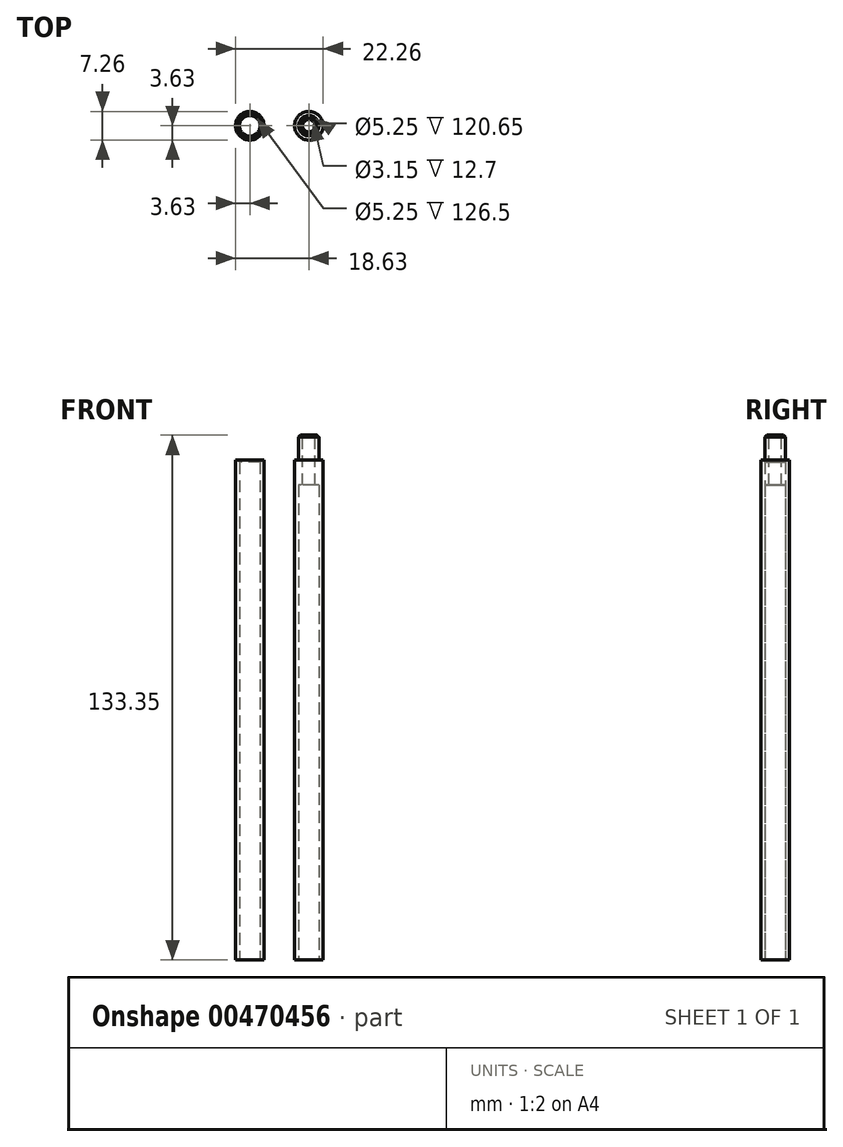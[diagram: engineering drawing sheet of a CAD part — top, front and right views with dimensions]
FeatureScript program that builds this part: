
annotation { "Feature Type Name" : "Feature", "Feature Type Description" : "" }
export const myFeature = defineFeature(function(context is Context, id is Id, definition is map)
    precondition{}
    {
        {
            var Q0;
            Q0=qCreatedBy(makeId("Top.planeOp"),FACE);
            var sketch = newSketch(context, id + "F0", { "sketchPlane" : qUnion([Q0])});
            skCircle(sketch, "E0", {"center": v(7.5, 0) * mm, "radius": 2.62 * mm});
            skCircle(sketch, "E1", {"center": v(-7.5, 0) * mm, "radius": 2.62 * mm});
            skCircle(sketch, "E2", {"center": v(-7.5, 0) * mm, "radius": 3.62 * mm});
            skCircle(sketch, "E3", {"center": v(7.5, 0) * mm, "radius": 3.62 * mm});
            skLineSegment(sketch, "E4", {"start": v(-7.5, 0) * mm, "end": v(7.5, 0) * mm, "construction": true});
            skSolve(sketch);
        }
        {
            var Q0;
            Q0 = qSketchRegion(id + "F0", true);
            extrude(context, id + "F1", {"entities" : qUnion([Q0]), "depth" : 127 * mm});
        }
        {
            var Q0;
            Q0=makeQuery(id+"F1.opExtrude","CAP_FACE",FACE,{"disambiguationData":[OSD([sQuery(id+"F0.wireOp",EDGE,"E0"),sQuery(id+"F0.wireOp",EDGE,"E3")])],"isStart":false});
            var sketch = newSketch(context, id + "F2", { "sketchPlane" : qUnion([Q0])});
            skCircle(sketch, "E5.0", {"center": v(7.5, 0) * mm, "radius": 2.62 * mm});
            skCircle(sketch, "E6", {"center": v(7.5, 0) * mm, "radius": 1.57 * mm});
            skSolve(sketch);
        }
        {
            var Q0;
            Q0 = qSketchRegion(id + "F2", true);
            extrude(context, id + "F3", {"entities" : qUnion([Q0]), "operationType" : NewBodyOperationType.ADD, "oppositeDirection" : true, "depth" : 6.35 * mm});
        }
        {
            var Q0;
            Q0=makeQuery(id+"F3.boolean.opBoolean","MERGE",FACE,{"derivedFrom":[makeQuery(id+"F1.opExtrude","CAP_FACE",FACE,{"disambiguationData":[OSD([sQuery(id+"F0.wireOp",EDGE,"E0"),sQuery(id+"F0.wireOp",EDGE,"E3")])],"isStart":false}),makeQuery(id+"F3.opExtrude","CAP_FACE",FACE,{"disambiguationData":[OSD([sQuery(id+"F2.wireOp",EDGE,"E5.0"),sQuery(id+"F2.wireOp",EDGE,"E6")])],"isStart":true})]});
            var sketch = newSketch(context, id + "F4", { "sketchPlane" : qUnion([Q0])});
            skCircle(sketch, "E7", {"center": v(7.5, 0) * mm, "radius": 2.58 * mm});
            skCircle(sketch, "E8.0", {"center": v(7.5, 0) * mm, "radius": 1.57 * mm});
            skSolve(sketch);
        }
        {
            var Q0;
            Q0 = qSketchRegion(id + "F4", true);
            extrude(context, id + "F5", {"entities" : qUnion([Q0]), "operationType" : NewBodyOperationType.ADD, "depth" : 6.35 * mm});
        }
        {
            var Q0;
            Q0=makeQuery(id+"F5.opExtrude","CAP_EDGE",EDGE,{"disambiguationData":[OSD([sQuery(id+"F4.wireOp",EDGE,"E7")])],"isStart":false});
            var Q1;
            Q1=makeQuery(id+"F1.opExtrude","CAP_EDGE",EDGE,{"disambiguationData":[OSD([sQuery(id+"F0.wireOp",EDGE,"E1")])],"isStart":false});
            chamfer(context, id + "F6", {"entities" : qUnion([Q0, Q1]), "width" : .5 * mm, "tangentPropagation" : true});
        }
    });
